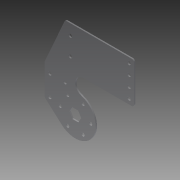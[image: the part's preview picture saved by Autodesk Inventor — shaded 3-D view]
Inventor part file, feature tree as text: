
AUTODESK INVENTOR PART (.ipt)
format: ipt  version: 2014 (Build 180170000, 170)  size: 165,888 bytes
history: native  units: in
note: dims shown in document units (in); Inventor stores cm internally (conversion verified against a paired STEP export)
features: extrude x2, fillet x1, sketch x1
ambient origin geometry x8: Origin, YZ Plane, XZ Plane, XY Plane, X Axis, Y Axis, Z Axis, Center Point
bodies: Solid1 (feature_tree)
feature tree (4):
  extrude  "Extrusion1"  Depth=0.125in
  extrude  "Extrusion2"  Depth=0.5in
  fillet  "Fillet2"  Radius=0.164in
  sketch  "Sketch2"  dims[d3=0.0625in d4=0.0in d7=0.625in d8=0.5in d23=0.164in d25=0.75in d26=0.0in d27=2.3622in d29=360.0deg d41=2.0in d42=0.75in d43=0.75in d44=1.5in d55=2.875in d57=0.17in d58=0.25in d59=0.25in d60=1.5748in d62=0.5in d63=0.3937in d65=1.0in d67=0.25in d68=1.444in d69=2.0in d70=1.5in d71=0.7833in d72=2.25in d76=2.2202in d78=0.25in d79=0.375in d82=0.7874in d84=0.75in d85=0.3937in d87=1.0in d91=1.25in d96=0.7874in d98=1.0in d99=0.3937in d101=1.0in d103=0.7874in d105=0.875in d106=0.3937in d108=1.0in d110=1.0in d111=1.0in d112=0.0in d113=0.25in d114=0.125in]
